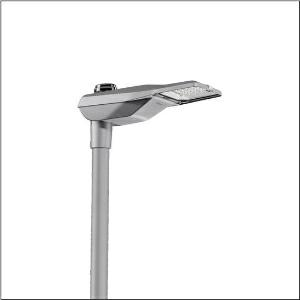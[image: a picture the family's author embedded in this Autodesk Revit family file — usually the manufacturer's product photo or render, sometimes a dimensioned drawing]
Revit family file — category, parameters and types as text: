
# Revit family: streetlight_sl_21_micro___st1_5a_5xe5p37n08cb_e60d
name_source: partatom
category: Lighting Fixtures
units: mm (PartAtom-declared; Revit-internal decimal feet)

## family parameters
Cut with Voids When Loaded = No
Host = Face
Light Source = No
Part Type = Normal
Room Calculation Point = No
Round Connector Dimension = Use Diameter
Shared = No

## types (1)
- --- (1 x LED, 2250 lm, 15.8 W, 3000K)
    Apparent Load = 16 VA
    CIE Flux Codes = 22 53 95 100 100
    Color Rendering = 70
    Color Temperature = 3000K
    Default Elevation = 1800 mm
    Description = Streetlight SL 21 micro, mast luminaire, primary light control with lens, of PMMA, primary optical cover: cover, of toughened safety glass, transparent, light distribution: ST1.5a, light emission: direct distribution, primary light characteristic: asymmetric, installation type: post-top, LED, 3G 1.5mm², High Power LED, rated luminous flux: 2.250lm, luminous efficacy: 142lm/W, light colour: 730, colour temperature: 3000K, control: overheat protection, presetting dimming linear, constant luminous flux control, time-dependent luminous flux control, flexible luminous flux parameterisation, mains connection: 230..240V, AC, 50/60Hz, connection cable pre-assembled, cable length: 6,5m, wiring characteristics: H07RN-F, start of lifetime: 16W, end of service life: 16W, reduction: 8W, luminaire housing, of diecast aluminium (EN AC-44300), powder-coated, Siteco® metallic grey (DB 702S), corrosivity category C5 mid according to DIN EN ISO 12944, multi-level sealing system, sealing non-destructively replaceable, inclination adjustable: 0°, 5°, 10°, 15°, length: 528mm, width: 235mm, height: 110mm, spigot size: 76/60mm (post-top), protection rating (complete): IP66, insulation class (complete): insulation class I (protective earthing), certification: CE, ENEC, ENEC+, VDE, impact resistance: IK09, permissible operating ambient temperature for outdoor applications: -40..+50°C, standard-compliant lighting for roads and squares, packaging unit: 1 piece

Light Distribution: ST1.5a
    Height = 110 mm
    Lamp = 1 x LED
    Lamp Light Flux = 2250 lm
    Lamp Power = 15.8 W
    Lamp count = 1
    Length = 528 mm
    Luminous efficacy = 142 lm/W
    Manufacturer = Siteco
    ModVariant = No
    Model = 5XE5P37N08CB
    Number of Poles = 1
    OnlyDefault = Yes
    Power Factor = 1
    Product Name = Streetlight SL 21 micro | ST1.5a
    Product group = mast luminaire | pylon top
    ProductGroupID = 6100
    Protection Class = Protection class I
    Protection Degree = IP 66
    RLX_Detail_Level = 1
    RLX_Emergency_Light_Flux = 0 lm
    RLX_Emergency_Type = 0
    RLX_Emergency_Type_DB = No
    RlxData = <blob elided: 102257 chars, md5=88e41697>
    Socket = socket
    Standby Power = 0 W
    System Light Flux = 2250 lm
    System Power = 16 W
    Type Comments = factory setting: luminous flux: 100 % | dim-lin: 254 | 300 mA
    Type Image = l_1294375.jpg
    URL = http://relux.com
    VarID = @adj_083181
    Voltage = 0 V
    Weight = 0.00 kg
    Width = 235 mm

## geometry (parser evidence)
native form markers: Blend x4, Sweep x10
no freeform markers — native parametric forms only
